AUTODESK INVENTOR PART (.ipt)
format: ipt  version: 2021 (Build 250183000, 183)  size: 348,160 bytes
history: native  units: mm
features: extrude x11, other x8, fillet x4, hole x1
ambient origin geometry x8: Origin, YZ Plane, XZ Plane, XY Plane, X Axis, Y Axis, Z Axis, Center Point
bodies: Body1 (feature_tree)
feature tree (24):
  other  "base_sketch"
  extrude  "base"  Depth=66.0mm
  extrude  "walls"  Depth=95.0mm
  extrude  "standoffs"  Depth=2.6mm
  fillet  "inside"  Radius=20.0mm
  fillet  "outside"  Radius=24.5mm
  fillet  "fillet_standoffs"  Radius=58.0mm
  extrude  "cutout_usbc_data"  Depth=87.0mm
  extrude  "cutout_usbc_pwr"  Depth=4.5mm
  extrude  "cutout_hdmi"  Depth=4.0mm
  fillet  "cutout_hdmi_fillet"  Radius=4.0mm
  extrude  "cutout_microsd"  Depth=4.0mm
  extrude  "cutout_flatflex"  Depth=4.0mm
  extrude  "cutout_flatflex_below"  Depth=4.0mm
  extrude  "cutout_microusb"  Depth=4.0mm
  extrude  "holes_mounting"  Depth=4.0mm
  other  "cutout_usbc_data_sketch"
  other  "cutout_usbc_pwr_sketch"
  other  "cutout_hdmi_sketch"
  other  "cutout_microsd_sketch"
  other  "cutout_flatflex_sketch"
  other  "cutout_flatflex_below_sketch"
  other  "cutout_microusb_sketch"
  hole  "holes_mounting_sketch"  [1 undecoded]
note: 1 required parameter value undecoded (feature->parameter linkage not recoverable at this tier; creation-order binding heuristic only, values carry confidence <= 0.55)
